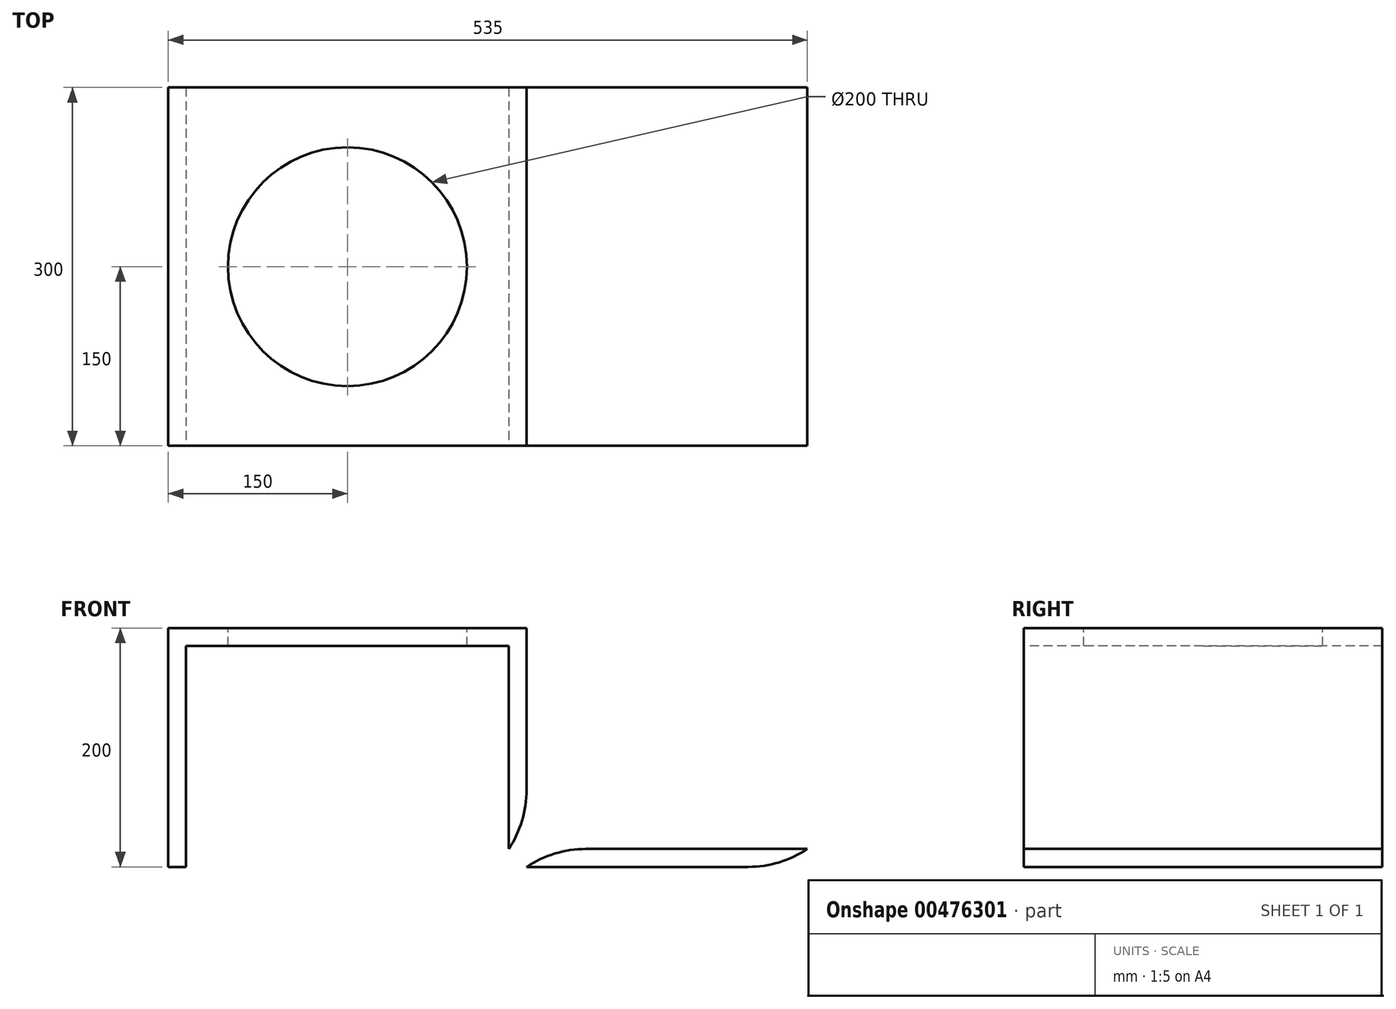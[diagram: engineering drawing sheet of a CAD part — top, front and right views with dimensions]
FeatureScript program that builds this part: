
annotation { "Feature Type Name" : "Feature", "Feature Type Description" : "" }
export const myFeature = defineFeature(function(context is Context, id is Id, definition is map)
    precondition{}
    {
        {
            var Q0;
            Q0=qCreatedBy(makeId("Front.planeOp"),FACE);
            var sketch = newSketch(context, id + "F0", { "sketchPlane" : qUnion([Q0])});
            skLineSegment(sketch, "E0.bottom", {"start": v(-285, 200) * mm, "end": v(15, 200) * mm});
            skLineSegment(sketch, "E0.top", {"start": v(-285, 185) * mm, "end": v(15, 185) * mm});
            skLineSegment(sketch, "E0.left", {"start": v(-285, 200) * mm, "end": v(-285, 185) * mm});
            skLineSegment(sketch, "E0.right", {"start": v(15, 200) * mm, "end": v(15, 185) * mm});
            skLineSegment(sketch, "E1.bottom", {"start": v(15, 200) * mm, "end": v(0, 200) * mm});
            skLineSegment(sketch, "E1.top", {"start": v(15, 0) * mm, "end": v(0, 0) * mm});
            skLineSegment(sketch, "E1.left", {"start": v(15, 200) * mm, "end": v(15, 0) * mm});
            skLineSegment(sketch, "E1.right", {"start": v(0, 200) * mm, "end": v(0, 0) * mm});
            skLineSegment(sketch, "E2.bottom", {"start": v(0, 0) * mm, "end": v(250, 0) * mm});
            skLineSegment(sketch, "E2.top", {"start": v(0, 15) * mm, "end": v(250, 15) * mm});
            skLineSegment(sketch, "E2.left", {"start": v(0, 0) * mm, "end": v(0, 15) * mm});
            skLineSegment(sketch, "E2.right", {"start": v(250, 0) * mm, "end": v(250, 15) * mm});
            skLineSegment(sketch, "E3.bottom", {"start": v(-285, 200) * mm, "end": v(-270, 200) * mm});
            skLineSegment(sketch, "E3.top", {"start": v(-285, 0) * mm, "end": v(-270, 0) * mm});
            skLineSegment(sketch, "E3.left", {"start": v(-285, 200) * mm, "end": v(-285, 0) * mm});
            skLineSegment(sketch, "E3.right", {"start": v(-270, 200) * mm, "end": v(-270, 0) * mm});
            skSolve(sketch);
        }
        {
            var Q0;
            {var subQ0=sQuery(id+"F0.wireOp",EDGE,"E0.bottom");Q0=makeQuery(id+"F0.imprint","IMPRINT",FACE,{"disambiguationData":[TD([[makeQuery(id+"F0.imprint","IMPRINT",EDGE,{"derivedFrom":subQ0}),-1.0]])]});}
            var Q1;
            {var subQ5=sQuery(id+"F0.wireOp",EDGE,"E2.right");Q1=makeQuery(id+"F0.imprint","IMPRINT",FACE,{"disambiguationData":[TD([[makeQuery(id+"F0.imprint","IMPRINT",EDGE,{"derivedFrom":subQ5}),1.0]])]});}
            var Q2;
            {var subQ5=sQuery(id+"F0.wireOp",EDGE,"E3.top");Q2=makeQuery(id+"F0.imprint","IMPRINT",FACE,{"disambiguationData":[TD([[makeQuery(id+"F0.imprint","IMPRINT",EDGE,{"derivedFrom":subQ5}),1.0]])]});}
            var Q3;
            {var subQ5=sQuery(id+"F0.wireOp",EDGE,"E2.left");Q3=makeQuery(id+"F0.imprint","IMPRINT",FACE,{"disambiguationData":[TD([[makeQuery(id+"F0.imprint","IMPRINT",EDGE,{"derivedFrom":subQ5}),-1.0]])]});}
            var Q4;
            {var subQ0=sQuery(id+"F0.wireOp",EDGE,"E1.left");var subQ1=sQuery(id+"F0.wireOp",EDGE,"E0.top");var subQ2=makeQuery(id+"F0.imprint","INTERSECT",VERTEX,{"derivedFrom":[subQ1,subQ0]});Q4=makeQuery(id+"F0.imprint","IMPRINT",FACE,{"disambiguationData":[TD([[makeQuery(id+"F0.imprint","IMPRINT",EDGE,{"disambiguationData":[TD([[subQ2,1.0]])],"derivedFrom":subQ1}),-1.0]])]});}
            var Q5;
            {var subQ5=sQuery(id+"F0.wireOp",EDGE,"E1.bottom");Q5=makeQuery(id+"F0.imprint","IMPRINT",FACE,{"disambiguationData":[TD([[makeQuery(id+"F0.imprint","IMPRINT",EDGE,{"derivedFrom":subQ5}),1.0]])]});}
            var Q6;
            {var subQ5=sQuery(id+"F0.wireOp",EDGE,"E3.bottom");Q6=makeQuery(id+"F0.imprint","IMPRINT",FACE,{"disambiguationData":[TD([[makeQuery(id+"F0.imprint","IMPRINT",EDGE,{"derivedFrom":subQ5}),-1.0]])]});}
            extrude(context, id + "F1", {"entities" : qUnion([Q0, Q1, Q2, Q3, Q4, Q5, Q6]), "oppositeDirection" : true, "depth" : 300 * mm});
        }
        {
            var Q0;
            Q0=makeQuery(id+"F1.opExtrude","SWEPT_FACE",FACE,{"disambiguationData":[OSD([sQuery(id+"F0.wireOp",EDGE,"E0.bottom"),sQuery(id+"F0.wireOp",EDGE,"E1.bottom"),sQuery(id+"F0.wireOp",EDGE,"E3.bottom")])]});
            var sketch = newSketch(context, id + "F2", { "sketchPlane" : qUnion([Q0])});
            skLineSegment(sketch, "E4", {"start": v(-285, 300) * mm, "end": v(15, 0) * mm, "construction": true});
            skLineSegment(sketch, "E5", {"start": v(15, 300) * mm, "end": v(-285, 0) * mm, "construction": true});
            skCircle(sketch, "E6", {"center": v(-135, 150) * mm, "radius": 100 * mm});
            skSolve(sketch);
        }
        {
            var Q0;
            Q0=makeQuery(id+"F2.imprint","IMPRINT",FACE,{"disambiguationData":[TD([[makeQuery(id+"F2.imprint","IMPRINT",EDGE,{"derivedFrom":sQuery(id+"F2.wireOp",EDGE,"E6")}),1.0]])]});
            extrude(context, id + "F3", {"entities" : qUnion([Q0]), "operationType" : NewBodyOperationType.REMOVE, "endBound" : BoundingType.UP_TO_NEXT, "oppositeDirection" : true, "depth" : 25 * mm});
        }
        {
            var Q0;
            Q0=makeQuery(id+"F1.opExtrude","SWEPT_EDGE",EDGE,{"disambiguationData":[OSD([sQuery(id+"F0.wireOp",EDGE,"E1.left"),sQuery(id+"F0.wireOp",EDGE,"E2.top")])]});
            var Q1;
            Q1=makeQuery(id+"F1.opExtrude","SWEPT_EDGE",EDGE,{"disambiguationData":[OSD([sQuery(id+"F0.wireOp",EDGE,"E2.bottom"),sQuery(id+"F0.wireOp",EDGE,"E2.left")])]});
            fillet(context, id + "F4", {"entities" : qUnion([Q0, Q1]), "radius" : 89.33 * mm, "tangentPropagation" : true, "allowEdgeOverflow" : false});
        }
    });
